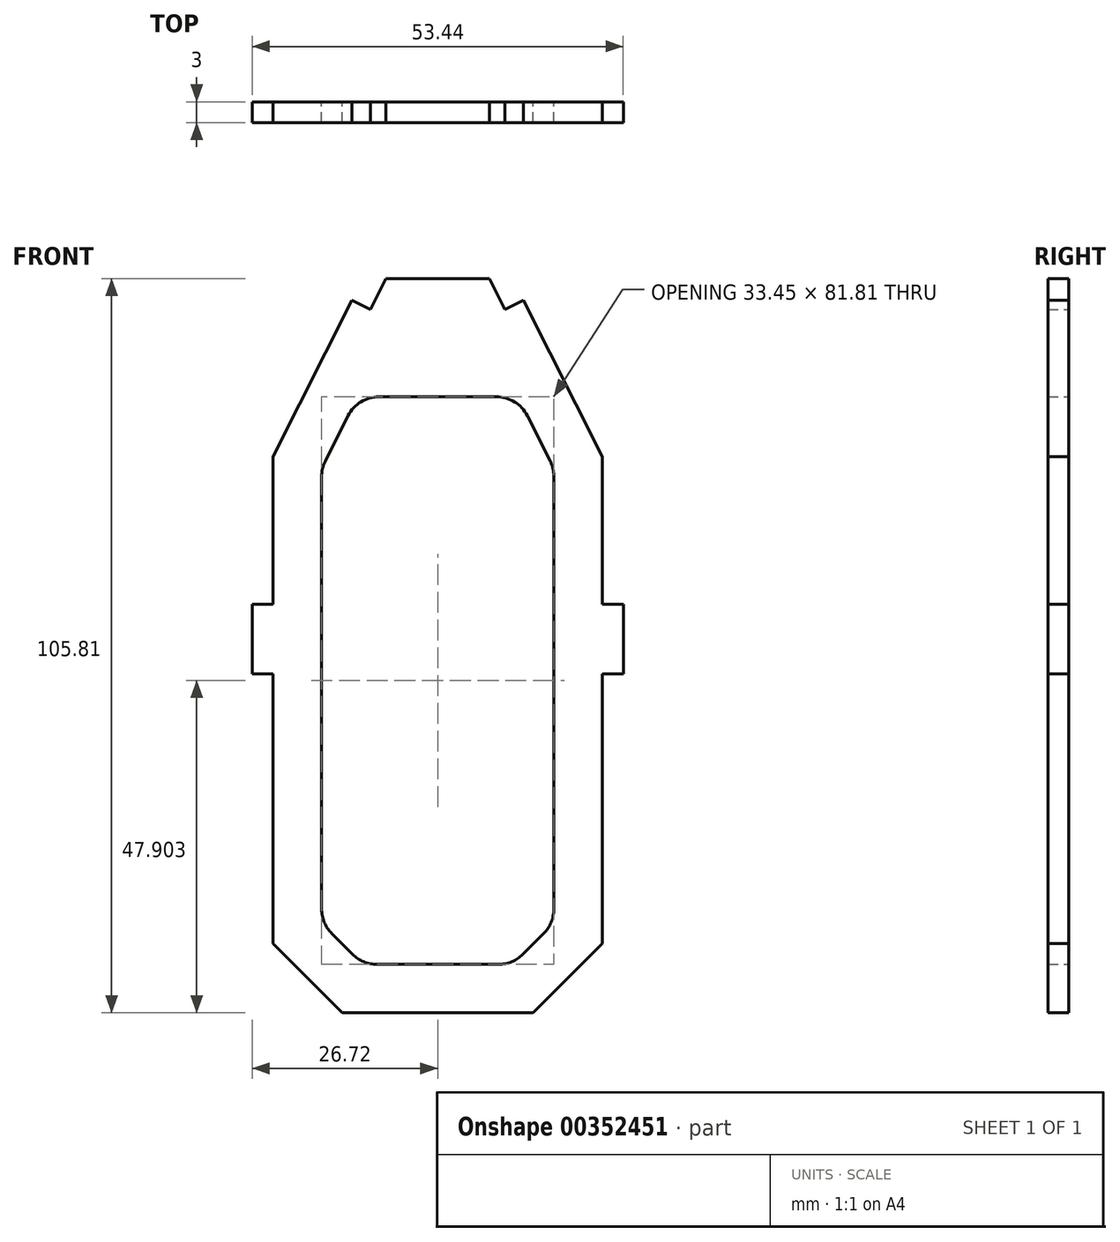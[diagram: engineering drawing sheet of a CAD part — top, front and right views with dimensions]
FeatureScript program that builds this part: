
annotation { "Feature Type Name" : "Feature", "Feature Type Description" : "" }
export const myFeature = defineFeature(function(context is Context, id is Id, definition is map)
    precondition{}
    {
        {
            var Q0;
            Q0=qCreatedBy(makeId("Front.planeOp"),FACE);
            var sketch = newSketch(context, id + "F0", { "sketchPlane" : qUnion([Q0])});
            skLineSegment(sketch, "E0.bottom", {"start": v(13.73, -53.87) * mm, "end": v(-13.72, -53.87) * mm});
            skLineSegment(sketch, "E0.top", {"start": v(7.44, 51.94) * mm, "end": v(-7.44, 51.94) * mm});
            skLineSegment(sketch, "E0.left", {"start": v(23.73, -43.87) * mm, "end": v(23.73, -5) * mm});
            skLineSegment(sketch, "E0.right", {"start": v(-23.72, -43.87) * mm, "end": v(-23.73, -5) * mm});
            skPoint(sketch, "E0.middle", {"position": v(0, 0) * mm});
            skPoint(sketch, "E1", {"position": v(-23.72, -43.87) * mm});
            skPoint(sketch, "E2", {"position": v(-13.72, -53.87) * mm});
            skLineSegment(sketch, "E3", {"start": v(-23.73, -43.87) * mm, "end": v(-13.72, -53.87) * mm});
            skLineSegment(sketch, "E4", {"start": v(0, 52.83) * mm, "end": v(0, -53.87) * mm, "construction": true});
            skLineSegment(sketch, "E5.MirrorCS", {"start": v(23.73, -43.87) * mm, "end": v(13.73, -53.87) * mm});
            skLineSegment(sketch, "E6", {"start": v(-23.73, 26.28) * mm, "end": v(-12.37, 48.82) * mm});
            skLineSegment(sketch, "E7", {"start": v(-12.37, 48.82) * mm, "end": v(-9.7, 47.47) * mm});
            skLineSegment(sketch, "E8", {"start": v(-9.7, 47.47) * mm, "end": v(-7.44, 51.94) * mm});
            skLineSegment(sketch, "E9.MirrorCS", {"start": v(9.7, 47.47) * mm, "end": v(7.44, 51.94) * mm});
            skLineSegment(sketch, "E10.MirrorCS", {"start": v(12.37, 48.82) * mm, "end": v(9.7, 47.47) * mm});
            skLineSegment(sketch, "E11.MirrorCS", {"start": v(23.72, 26.28) * mm, "end": v(12.37, 48.82) * mm});
            skLineSegment(sketch, "E12.0", {"start": v(-15.26, -42.44) * mm, "end": v(-12.29, -45.4) * mm});
            skLineSegment(sketch, "E12.4", {"start": v(-16.2, 25.68) * mm, "end": v(-12.91, 32.19) * mm});
            skLineSegment(sketch, "E12.6", {"start": v(-16.73, -38.9) * mm, "end": v(-16.73, 23.43) * mm});
            skLineSegment(sketch, "E12.8", {"start": v(16.2, 25.68) * mm, "end": v(12.91, 32.19) * mm});
            skLineSegment(sketch, "E12.9", {"start": v(16.73, -38.9) * mm, "end": v(16.73, 23.43) * mm});
            skLineSegment(sketch, "E12.10", {"start": v(15.26, -42.44) * mm, "end": v(12.29, -45.4) * mm});
            skLineSegment(sketch, "E12.11", {"start": v(8.75, -46.87) * mm, "end": v(-8.75, -46.87) * mm});
            skLineSegment(sketch, "E13", {"start": v(-8.45, 34.94) * mm, "end": v(8.45, 34.94) * mm});
            skPoint(sketch, "E14.visualSharp", {"position": v(-11.53, 34.94) * mm});
            skArc(sketch, "E14.filletArc", {"start": v(-8.45, 34.94) * mm, "mid": v(-11.07, 34.2) * mm, "end": v(-12.91, 32.19) * mm});
            skPoint(sketch, "E15.visualSharp", {"position": v(-16.73, 24.61) * mm});
            skArc(sketch, "E15.filletArc", {"start": v(-16.2, 25.68) * mm, "mid": v(-16.59, 24.58) * mm, "end": v(-16.73, 23.43) * mm});
            skPoint(sketch, "E16.visualSharp", {"position": v(11.53, 34.94) * mm});
            skArc(sketch, "E16.filletArc", {"start": v(12.91, 32.19) * mm, "mid": v(11.07, 34.2) * mm, "end": v(8.45, 34.94) * mm});
            skPoint(sketch, "E17.visualSharp", {"position": v(16.72, 24.61) * mm});
            skArc(sketch, "E17.filletArc", {"start": v(16.73, 23.43) * mm, "mid": v(16.59, 24.58) * mm, "end": v(16.2, 25.68) * mm});
            skPoint(sketch, "E18.visualSharp", {"position": v(-16.73, -40.97) * mm});
            skArc(sketch, "E18.filletArc", {"start": v(-16.72, -38.9) * mm, "mid": v(-16.34, -40.81) * mm, "end": v(-15.26, -42.44) * mm});
            skPoint(sketch, "E19.visualSharp", {"position": v(-10.83, -46.87) * mm});
            skArc(sketch, "E19.filletArc", {"start": v(-12.29, -45.4) * mm, "mid": v(-10.67, -46.5) * mm, "end": v(-8.75, -46.87) * mm});
            skPoint(sketch, "E20.visualSharp", {"position": v(10.83, -46.87) * mm});
            skArc(sketch, "E20.filletArc", {"start": v(8.75, -46.87) * mm, "mid": v(10.67, -46.5) * mm, "end": v(12.29, -45.4) * mm});
            skPoint(sketch, "E21.visualSharp", {"position": v(16.73, -40.97) * mm});
            skArc(sketch, "E21.filletArc", {"start": v(15.26, -42.44) * mm, "mid": v(16.34, -40.81) * mm, "end": v(16.73, -38.9) * mm});
            skLineSegment(sketch, "E22", {"start": v(-23.73, -5) * mm, "end": v(-26.73, -5) * mm});
            skLineSegment(sketch, "E23", {"start": v(-26.72, -5) * mm, "end": v(-26.72, 5) * mm});
            skLineSegment(sketch, "E24", {"start": v(-26.73, 5) * mm, "end": v(-23.73, 5) * mm});
            skLineSegment(sketch, "E25.trimOffspring", {"start": v(-23.73, 5) * mm, "end": v(-23.73, 26.28) * mm});
            skLineSegment(sketch, "E26.MirrorCS", {"start": v(26.73, 5) * mm, "end": v(23.73, 5) * mm});
            skLineSegment(sketch, "E27.MirrorCS", {"start": v(26.72, -5) * mm, "end": v(26.72, 5) * mm});
            skLineSegment(sketch, "E28.MirrorCS", {"start": v(23.73, -5) * mm, "end": v(26.73, -5) * mm});
            skLineSegment(sketch, "E29.trimOffspring", {"start": v(23.73, 5) * mm, "end": v(23.73, 26.28) * mm});
            skSolve(sketch);
        }
        {
            var Q0;
            Q0 = qSketchRegion(id + "F0", true);
            extrude(context, id + "F1", {"entities" : qUnion([Q0]), "depth" : 3 * mm, "symmetric" : true});
        }
    });
